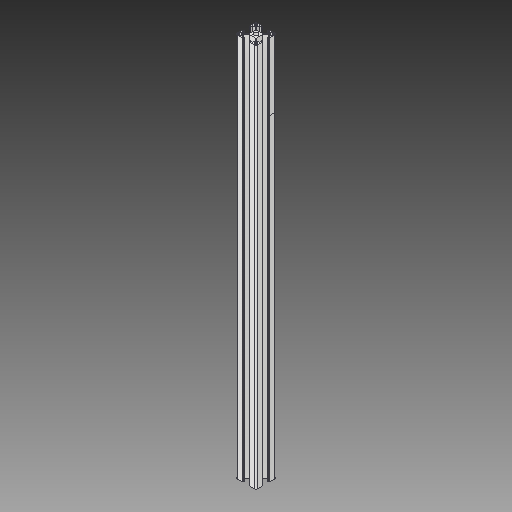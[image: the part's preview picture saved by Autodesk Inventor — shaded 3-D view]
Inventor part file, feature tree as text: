
AUTODESK INVENTOR PART (.ipt)
format: ipt  version: 2019 (Build 230136000, 136)  size: 310,272 bytes
history: native  units: in
note: dims shown in document units (in); Inventor stores cm internally (conversion verified against a paired STEP export)
features: extrude x1, sketch x1, projected_geometry x1
ambient origin geometry x8: Origin, YZ Plane, XZ Plane, XY Plane, X Axis, Y Axis, Z Axis, Center Point
bodies: Solid1 (feature_tree), Body1 (feature_tree)
feature tree (3):
  extrude  "Extrusion1"  [1 undecoded]
  sketch  "Sketch1"  dims[d0=18.5433in d1=0.0in]
  projected_geometry  "Projected Loop1"
note: 1 required parameter value undecoded (feature->parameter linkage not recoverable at this tier; creation-order binding heuristic only, values carry confidence <= 0.55)
